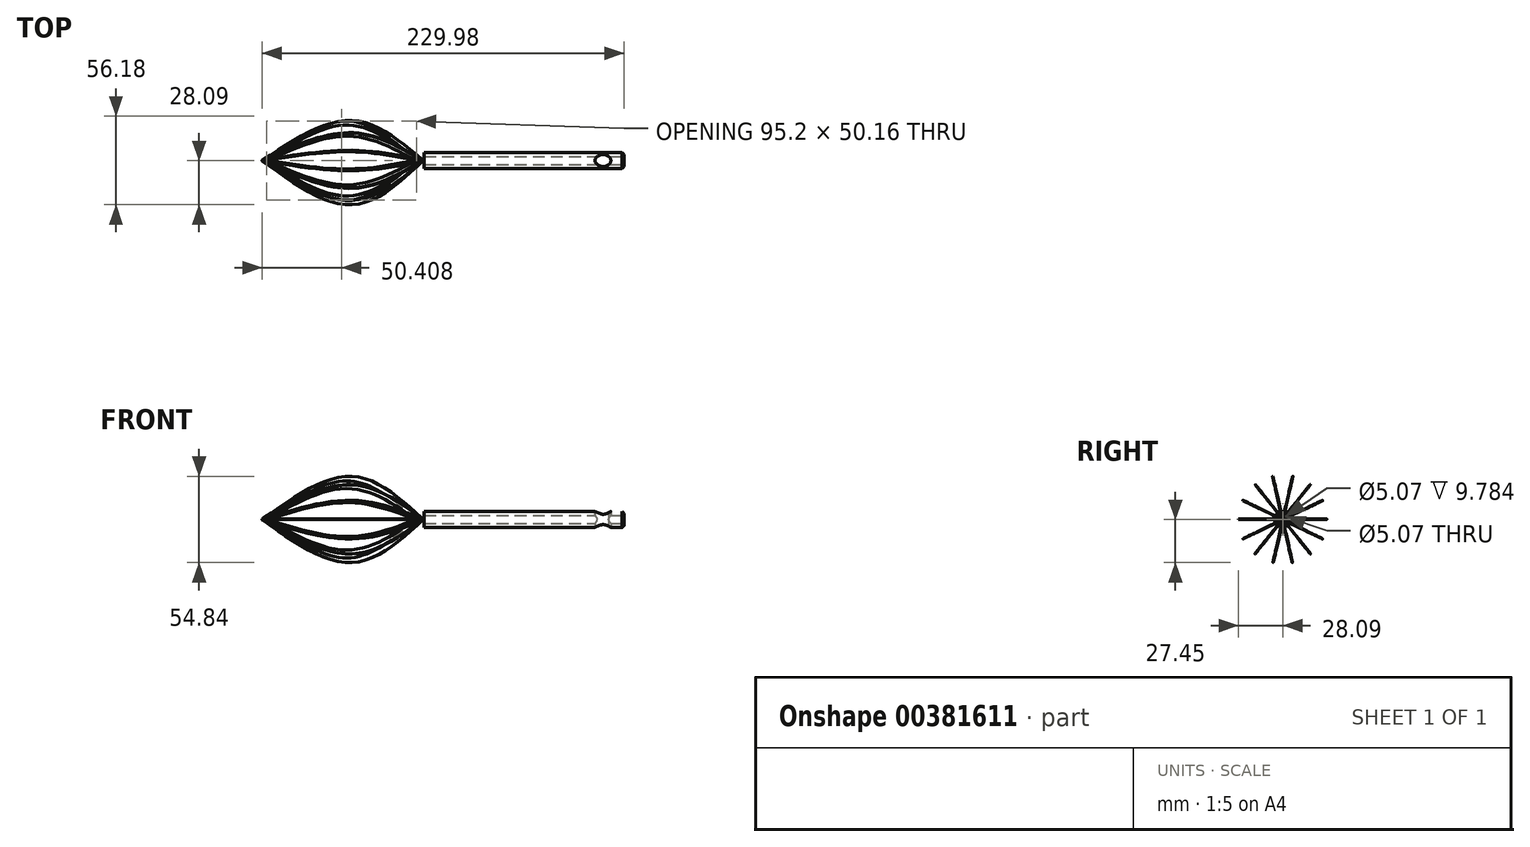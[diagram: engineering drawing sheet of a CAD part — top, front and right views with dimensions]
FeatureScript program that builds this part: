
annotation { "Feature Type Name" : "Feature", "Feature Type Description" : "" }
export const myFeature = defineFeature(function(context is Context, id is Id, definition is map)
    precondition{}
    {
        {
            var Q0;
            Q0=qCreatedBy(makeId("Right.planeOp"),FACE);
            var sketch = newSketch(context, id + "F0", { "sketchPlane" : qUnion([Q0])});
            skCircle(sketch, "E0", {"center": v(0, 0) * mm, "radius": 5.08 * mm});
            skSolve(sketch);
        }
        {
            var Q0;
            Q0=makeQuery(id+"F0.imprint","IMPRINT",FACE,{"disambiguationData":[TD([[makeQuery(id+"F0.imprint","IMPRINT",EDGE,{"derivedFrom":sQuery(id+"F0.wireOp",EDGE,"E0")}),1.0]])]});
            extrude(context, id + "F1", {"entities" : qUnion([Q0]), "oppositeDirection" : true, "depth" : 127 * mm});
        }
        {
            var Q0;
            Q0=qCreatedBy(makeId("Top.planeOp"),FACE);
            var sketch = newSketch(context, id + "F2", { "sketchPlane" : qUnion([Q0])});
            skFitSpline(sketch, "E1", {"points": [v(-18.53, 0) * mm, v(-12.94, 3.73) * mm, v(-8.43, 0) * mm, v(-13.25, -3.88) * mm, v(-18.53, 0) * mm]});
            skFitSpline(sketch, "E2.MirrorC", {"points": [v(-18.53, 0) * mm, v(-12.94, -3.73) * mm, v(-8.43, 0) * mm, v(-13.25, 3.88) * mm, v(-18.53, 0) * mm]});
            skSolve(sketch);
        }
        {
            var Q0;
            Q0 = qSketchRegion(id + "F2", true);
            extrude(context, id + "F3", {"entities" : qUnion([Q0]), "operationType" : NewBodyOperationType.REMOVE, "depth" : 175.5 * mm});
        }
        {
            var Q0;
            Q0 = qSketchRegion(id + "F2", true);
            extrude(context, id + "F4", {"entities" : qUnion([Q0]), "operationType" : NewBodyOperationType.REMOVE, "oppositeDirection" : true, "depth" : 128270 * mm});
        }
        {
            var Q0;
            Q0=qCreatedBy(makeId("Right.planeOp"),FACE);
            var sketch = newSketch(context, id + "F5", { "sketchPlane" : qUnion([Q0])});
            skCircle(sketch, "E3", {"center": v(0, 0) * mm, "radius": 2.53 * mm});
            skSolve(sketch);
        }
        {
            var Q0;
            Q0 = qSketchRegion(id + "F5", true);
            extrude(context, id + "F6", {"entities" : qUnion([Q0]), "operationType" : NewBodyOperationType.REMOVE, "oppositeDirection" : true, "depth" : 154.43 * mm});
        }
        {
            var Q0;
            Q0=makeQuery(id+"F1.opExtrude","CAP_EDGE",EDGE,{"disambiguationData":[OSD([sQuery(id+"F0.wireOp",EDGE,"E0")])],"isStart":true});
            chamfer(context, id + "F7", {"entities" : qUnion([Q0]), "width" : 1.27 * mm, "tangentPropagation" : true});
        }
        {
            var Q0;
            Q0=qCreatedBy(makeId("Top.planeOp"),FACE);
            var sketch = newSketch(context, id + "F8", { "sketchPlane" : qUnion([Q0])});
            skLineSegment(sketch, "E4", {"start": v(-71.16, 0) * mm, "end": v(-230.17, 0) * mm});
            skSolve(sketch);
        }
        {
            var Q0;
            Q0=qCreatedBy(makeId("Top.planeOp"),FACE);
            var sketch = newSketch(context, id + "F9", { "sketchPlane" : qUnion([Q0])});
            skFitSpline(sketch, "E5", {"points": [v(-127.67, 0) * mm, v(-172.75, 28.05) * mm, v(-229.98, 0) * mm], "startDerivative": vector(-90.88, 85.62) * mm, "endDerivative": vector(-113.39, -83.06) * mm});
            skFitSpline(sketch, "E6.MirrorCS", {"points": [v(-127.67, 0) * mm, v(-172.75, -28.05) * mm, v(-229.98, 0) * mm], "startDerivative": vector(-90.88, -85.62) * mm, "endDerivative": vector(-113.39, 83.06) * mm});
            skSolve(sketch);
        }
        {
            var Q0;
            Q0=makeQuery(id+"F9.imprint","IMPRINT",FACE,{"disambiguationData":[TD([[makeQuery(id+"F9.imprint","IMPRINT",EDGE,{"derivedFrom":sQuery(id+"F9.wireOp",EDGE,"E5")}),1.0]])]});
            extrude(context, id + "F10", {"entities" : qUnion([Q0]), "depth" : 0.25 * mm});
        }
        {
            var Q0;
            Q0=makeQuery(id+"F10.opExtrude","CAP_FACE",FACE,{"disambiguationData":[OSD([sQuery(id+"F9.wireOp",EDGE,"E5"),sQuery(id+"F9.wireOp",EDGE,"E6.MirrorCS")])],"isStart":false});
            var sketch = newSketch(context, id + "F11", { "sketchPlane" : qUnion([Q0])});
            skFitSpline(sketch, "E7", {"points": [v(-131.97, 0) * mm, v(-174.99, 25.06) * mm, v(-227.17, 0) * mm], "startDerivative": vector(-86.71, 76.24) * mm, "endDerivative": vector(-103.47, -74.35) * mm});
            skFitSpline(sketch, "E8.MirrorCS", {"points": [v(-131.97, 0) * mm, v(-174.99, -25.06) * mm, v(-227.17, 0) * mm], "startDerivative": vector(-86.71, -76.24) * mm, "endDerivative": vector(-103.47, 74.35) * mm});
            skSolve(sketch);
        }
        {
            var Q0;
            Q0 = qSketchRegion(id + "F11", true);
            extrude(context, id + "F12", {"entities" : qUnion([Q0]), "operationType" : NewBodyOperationType.REMOVE, "oppositeDirection" : true, "depth" : 25.4 * mm});
        }
        {
            var Q0;
            Q0=makeQuery(id+"F10.opExtrude","SWEPT_BODY",BODY,{"disambiguationData":[OSD([sQuery(id+"F9.wireOp",EDGE,"E5"),sQuery(id+"F9.wireOp",EDGE,"E6.MirrorCS")])]});
            var Q1;
            Q1=sQuery(id+"F8.wireOp",EDGE,"E4");
            circularPattern(context, id + "F13", {"entities" : qUnion([Q0]), "axis" : qUnion([Q1]), "angle" : 360 * degree, "instanceCount" : 7, "equalSpace" : true});
        }
    });
